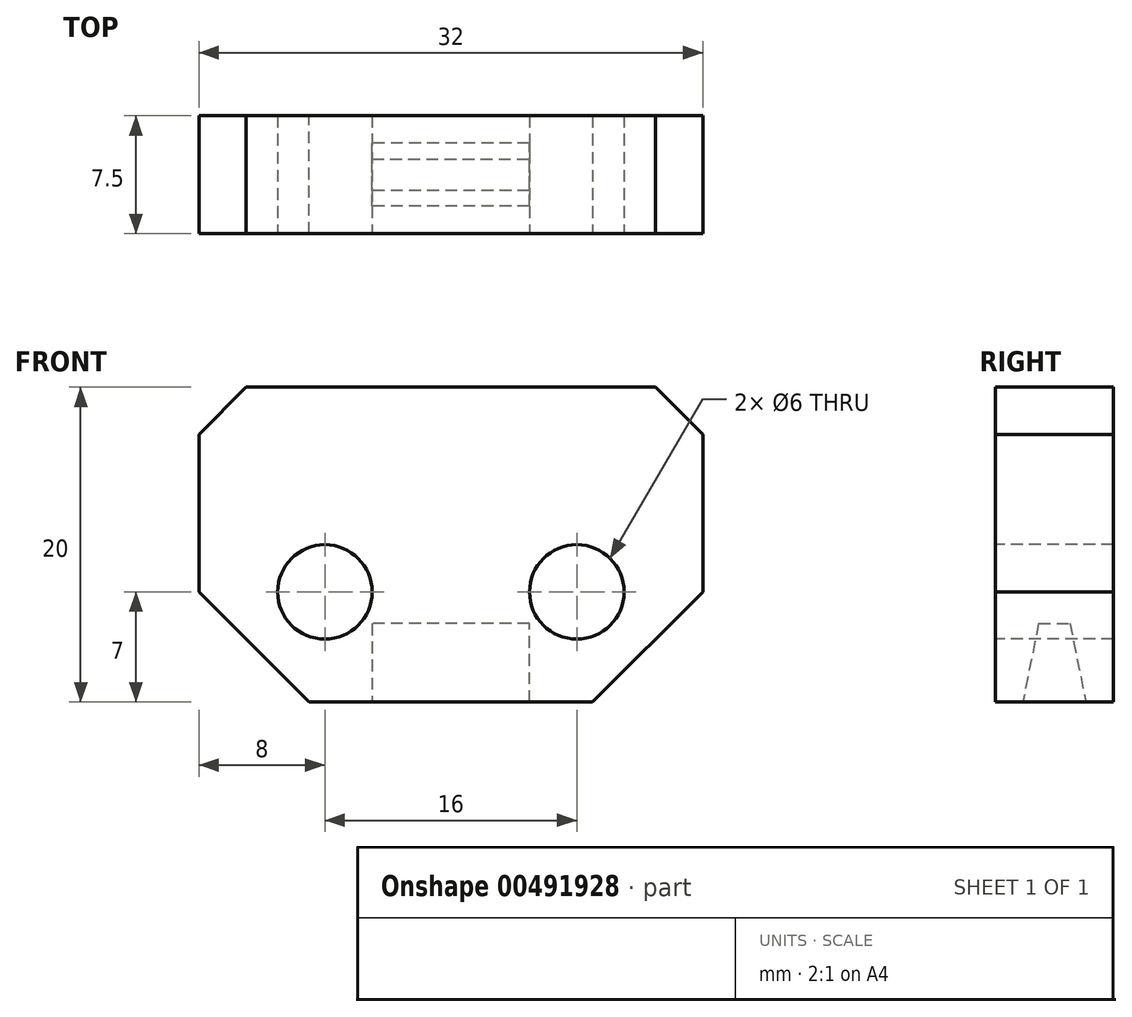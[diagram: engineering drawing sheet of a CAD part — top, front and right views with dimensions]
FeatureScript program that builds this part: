
annotation { "Feature Type Name" : "Feature", "Feature Type Description" : "" }
export const myFeature = defineFeature(function(context is Context, id is Id, definition is map)
    precondition{}
    {
        {
            assignVariable(context, id + "F0", {"name" : "depth", "anyValue" : 7.5});
        }
        {
            var Q0;
            Q0=qCreatedBy(makeId("Front.planeOp"),FACE);
            var sketch = newSketch(context, id + "F1", { "sketchPlane" : qUnion([Q0])});
            skLineSegment(sketch, "E0.bottom", {"start": v(-16, 10) * mm, "end": v(16, 10) * mm});
            skLineSegment(sketch, "E0.top", {"start": v(-16, -10) * mm, "end": v(16, -10) * mm});
            skLineSegment(sketch, "E0.left", {"start": v(-16, 10) * mm, "end": v(-16, -10) * mm});
            skLineSegment(sketch, "E0.right", {"start": v(16, 10) * mm, "end": v(16, -10) * mm});
            skPoint(sketch, "E0.middle", {"position": v(0, 0) * mm});
            skSolve(sketch);
        }
        {
            var Q0;
            Q0=makeQuery(id+"F1.imprint","IMPRINT",FACE,{"disambiguationData":[TD([[makeQuery(id+"F1.imprint","IMPRINT",EDGE,{"derivedFrom":sQuery(id+"F1.wireOp",EDGE,"E0.bottom")}),-1.0]])]});
            extrude(context, id + "F2", {"entities" : qUnion([Q0]), "depth" : (getVariable(context, 'depth')) * mm});
        }
        {
            var Q0;
            Q0=makeQuery(id+"F2.opExtrude","SWEPT_EDGE",EDGE,{"disambiguationData":[OSD([sQuery(id+"F1.wireOp",EDGE,"E0.top"),sQuery(id+"F1.wireOp",EDGE,"E0.left")])]});
            var Q1;
            Q1=makeQuery(id+"F2.opExtrude","SWEPT_EDGE",EDGE,{"disambiguationData":[OSD([sQuery(id+"F1.wireOp",EDGE,"E0.top"),sQuery(id+"F1.wireOp",EDGE,"E0.right")])]});
            chamfer(context, id + "F3", {"entities" : qUnion([Q0, Q1]), "width" : 7 * mm, "tangentPropagation" : true});
        }
        {
            var Q0;
            Q0=makeQuery(id+"F2.opExtrude","CAP_FACE",FACE,{"disambiguationData":[OSD([sQuery(id+"F1.wireOp",EDGE,"E0.bottom"),sQuery(id+"F1.wireOp",EDGE,"E0.top"),sQuery(id+"F1.wireOp",EDGE,"E0.left"),sQuery(id+"F1.wireOp",EDGE,"E0.right")])],"isStart":false});
            var sketch = newSketch(context, id + "F4", { "sketchPlane" : qUnion([Q0])});
            skCircle(sketch, "E1", {"center": v(-8, -3) * mm, "radius": 3 * mm});
            skCircle(sketch, "E2", {"center": v(8, -3) * mm, "radius": 3 * mm});
            skSolve(sketch);
        }
        {
            var Q0;
            Q0=makeQuery(id+"F4.imprint","IMPRINT",FACE,{"disambiguationData":[TD([[makeQuery(id+"F4.imprint","IMPRINT",EDGE,{"derivedFrom":sQuery(id+"F4.wireOp",EDGE,"E1")}),1.0]])]});
            var Q1;
            Q1=makeQuery(id+"F4.imprint","IMPRINT",FACE,{"disambiguationData":[TD([[makeQuery(id+"F4.imprint","IMPRINT",EDGE,{"derivedFrom":sQuery(id+"F4.wireOp",EDGE,"E2")}),1.0]])]});
            extrude(context, id + "F5", {"entities" : qUnion([Q0, Q1]), "operationType" : NewBodyOperationType.REMOVE, "oppositeDirection" : true, "depth" : 25 * mm});
        }
        {
            var Q0;
            Q0=makeQuery(id+"F2.opExtrude","SWEPT_EDGE",EDGE,{"disambiguationData":[OSD([sQuery(id+"F1.wireOp",EDGE,"E0.bottom"),sQuery(id+"F1.wireOp",EDGE,"E0.right")])]});
            var Q1;
            Q1=makeQuery(id+"F2.opExtrude","SWEPT_EDGE",EDGE,{"disambiguationData":[OSD([sQuery(id+"F1.wireOp",EDGE,"E0.bottom"),sQuery(id+"F1.wireOp",EDGE,"E0.left")])]});
            chamfer(context, id + "F6", {"entities" : qUnion([Q0, Q1]), "width" : 3 * mm, "tangentPropagation" : true});
        }
        {
            var Q0;
            Q0=makeQuery(id+"F2.opExtrude","SWEPT_FACE",FACE,{"disambiguationData":[OSD([sQuery(id+"F1.wireOp",EDGE,"E0.top")])]});
            var sketch = newSketch(context, id + "F7", { "sketchPlane" : qUnion([Q0])});
            skLineSegment(sketch, "E3", {"start": v(-5, 3.75) * mm, "end": v(5, 3.75) * mm});
            skPoint(sketch, "E3.startSnap0", {"position": v(-9, 3.75) * mm});
            skPoint(sketch, "E4", {"position": v(0, 3.75) * mm});
            skPoint(sketch, "E5", {"position": v(0, 7.5) * mm});
            skLineSegment(sketch, "E6.bottom", {"start": v(5, 5.75) * mm, "end": v(-5, 5.75) * mm});
            skLineSegment(sketch, "E6.top", {"start": v(5, 1.75) * mm, "end": v(-5, 1.75) * mm});
            skLineSegment(sketch, "E6.left", {"start": v(5, 5.75) * mm, "end": v(5, 1.75) * mm});
            skLineSegment(sketch, "E6.right", {"start": v(-5, 5.75) * mm, "end": v(-5, 1.75) * mm});
            skSolve(sketch);
        }
        {
            var Q0;
            Q0 = qSketchRegion(id + "F7", true);
            extrude(context, id + "F8", {"entities" : qUnion([Q0]), "operationType" : NewBodyOperationType.REMOVE, "oppositeDirection" : true, "depth" : 5 * mm, "offsetDistance" : 25 * mm});
        }
        {
            var Q0;
            Q0=makeQuery(id+"F8.boolean.opBoolean","COPY",EDGE,{"derivedFrom":makeQuery(id+"F8.opExtrude","CAP_EDGE",EDGE,{"disambiguationData":[OSD([sQuery(id+"F7.wireOp",EDGE,"E6.top")])],"isStart":false})});
            var Q1;
            Q1=makeQuery(id+"F8.boolean.opBoolean","COPY",EDGE,{"derivedFrom":makeQuery(id+"F8.opExtrude","CAP_EDGE",EDGE,{"disambiguationData":[OSD([sQuery(id+"F7.wireOp",EDGE,"E6.bottom")])],"isStart":false})});
            chamfer(context, id + "F9", {"entities" : qUnion([Q0, Q1]), "chamferType" : ChamferType.TWO_OFFSETS, "width1" : 5 * mm, "oppositeDirection" : false, "width2" : 1 * mm, "tangentPropagation" : true});
        }
    });
